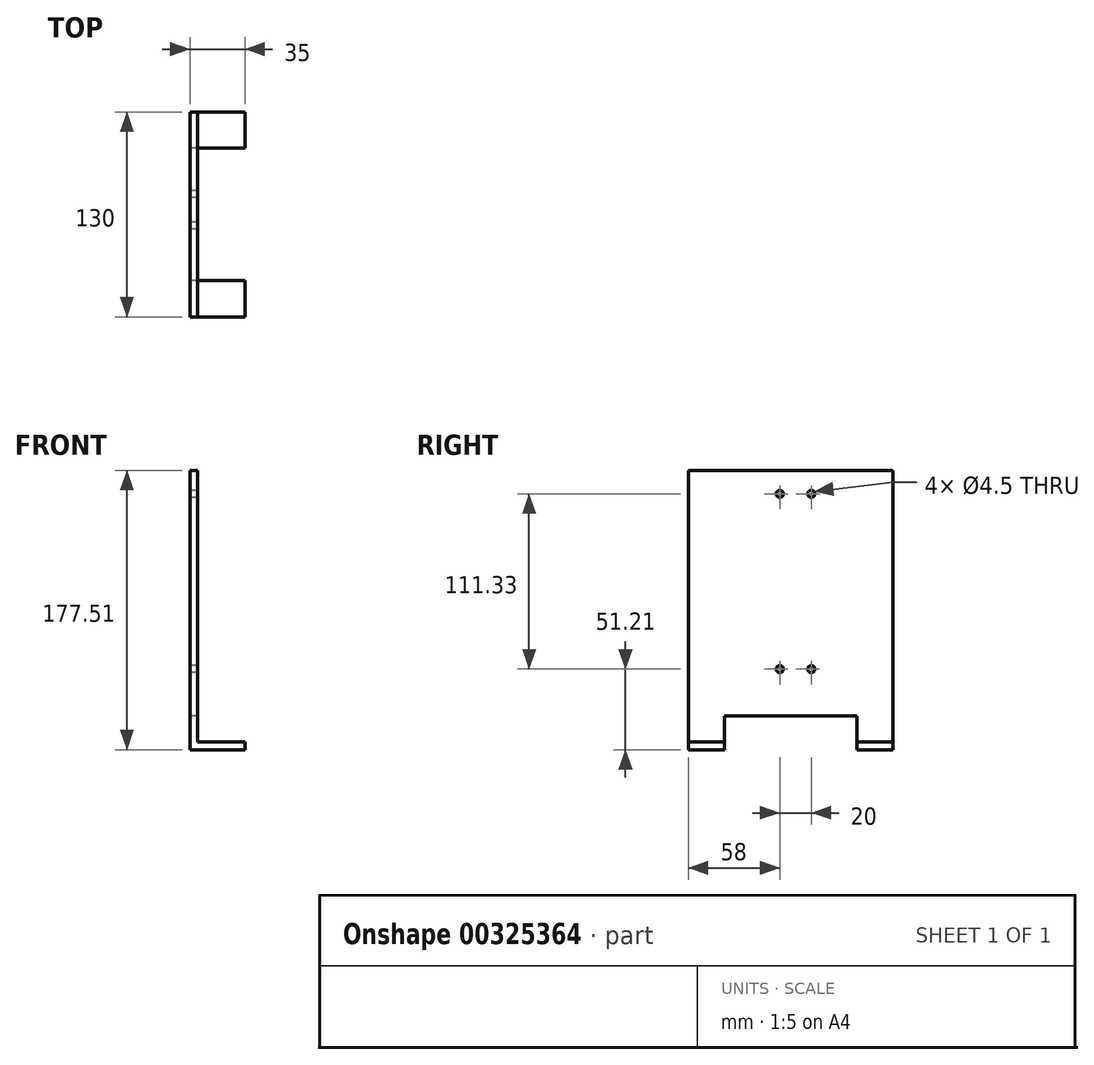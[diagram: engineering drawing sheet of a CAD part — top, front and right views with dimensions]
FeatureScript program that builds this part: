
annotation { "Feature Type Name" : "Feature", "Feature Type Description" : "" }
export const myFeature = defineFeature(function(context is Context, id is Id, definition is map)
    precondition{}
    {
        {
            var Q0;
            Q0=qCreatedBy(makeId("Right.planeOp"),FACE);
            var sketch = newSketch(context, id + "F0", { "sketchPlane" : qUnion([Q0])});
            skLineSegment(sketch, "E0.bottom", {"start": v(-38.4, 65.5) * mm, "end": v(32.4, 65.5) * mm, "construction": true});
            skLineSegment(sketch, "E0.top", {"start": v(-38.4, -65.5) * mm, "end": v(32.4, -65.5) * mm, "construction": true});
            skLineSegment(sketch, "E0.left", {"start": v(-48, 55.9) * mm, "end": v(-48, -55.9) * mm, "construction": true});
            skLineSegment(sketch, "E0.right", {"start": v(42, 55.9) * mm, "end": v(42, -55.9) * mm, "construction": true});
            skCircle(sketch, "E1", {"center": v(-10, 55.53) * mm, "radius": 2.25 * mm});
            skCircle(sketch, "E2", {"center": v(-10, -55.8) * mm, "radius": 2.25 * mm});
            skLineSegment(sketch, "E3", {"start": v(-10, 55.53) * mm, "end": v(-10, -55.8) * mm, "construction": true});
            skCircle(sketch, "E4.MirrorC", {"center": v(10, 55.53) * mm, "radius": 2.25 * mm});
            skCircle(sketch, "E5.MirrorC", {"center": v(10, -55.8) * mm, "radius": 2.25 * mm});
            skPoint(sketch, "E6.visualSharp", {"position": v(-48, 65.5) * mm});
            skArc(sketch, "E6.filletArc", {"start": v(-38.4, 65.5) * mm, "mid": v(-45.19, 62.69) * mm, "end": v(-48, 55.9) * mm, "construction": true});
            skPoint(sketch, "E7.visualSharp", {"position": v(42, -65.5) * mm});
            skArc(sketch, "E7.filletArc", {"start": v(32.4, -65.5) * mm, "mid": v(39.19, -62.69) * mm, "end": v(42, -55.9) * mm, "construction": true});
            skPoint(sketch, "E8.visualSharp", {"position": v(42, 65.5) * mm});
            skArc(sketch, "E8.filletArc", {"start": v(42, 55.9) * mm, "mid": v(39.19, 62.69) * mm, "end": v(32.4, 65.5) * mm, "construction": true});
            skPoint(sketch, "E9.visualSharp", {"position": v(-48, -65.5) * mm});
            skArc(sketch, "E9.filletArc", {"start": v(-48, -55.9) * mm, "mid": v(-45.19, -62.69) * mm, "end": v(-38.4, -65.5) * mm, "construction": true});
            skLineSegment(sketch, "E10.bottom", {"start": v(-68, 70.5) * mm, "end": v(62, 70.5) * mm});
            skLineSegment(sketch, "E10.top", {"start": v(-45.1, -85.5) * mm, "end": v(39.1, -85.5) * mm});
            skLineSegment(sketch, "E10.left", {"start": v(-68, 70.5) * mm, "end": v(-68, -85.5) * mm});
            skLineSegment(sketch, "E10.right", {"start": v(62, 70.5) * mm, "end": v(62, -85.5) * mm});
            skLineSegment(sketch, "E11.top", {"start": v(-68, -107) * mm, "end": v(-45.1, -107) * mm});
            skLineSegment(sketch, "E11.left", {"start": v(-68, -85.5) * mm, "end": v(-68, -107) * mm});
            skLineSegment(sketch, "E11.right", {"start": v(-45.1, -85.5) * mm, "end": v(-45.1, -107) * mm});
            skLineSegment(sketch, "E12", {"start": v(-3, -85.5) * mm, "end": v(-3, 70.5) * mm, "construction": true});
            skLineSegment(sketch, "E13.MirrorCS", {"start": v(62, -85.5) * mm, "end": v(62, -107) * mm});
            skLineSegment(sketch, "E14.MirrorCS", {"start": v(39.1, -85.5) * mm, "end": v(39.1, -107) * mm});
            skLineSegment(sketch, "E15.MirrorCS", {"start": v(62, -107) * mm, "end": v(39.1, -107) * mm});
            skSolve(sketch);
        }
        {
            var Q0;
            Q0=makeQuery(id+"F0.imprint","IMPRINT",FACE,{"disambiguationData":[TD([[makeQuery(id+"F0.imprint","IMPRINT",EDGE,{"derivedFrom":sQuery(id+"F0.wireOp",EDGE,"E1")}),-1.0]])]});
            extrude(context, id + "F1", {"entities" : qUnion([Q0]), "depth" : 5 * mm});
        }
        {
            var Q0;
            Q0=makeQuery(id+"F1.opExtrude","CAP_FACE",FACE,{"disambiguationData":[OSD([sQuery(id+"F0.wireOp",EDGE,"E1"),sQuery(id+"F0.wireOp",EDGE,"E2"),sQuery(id+"F0.wireOp",EDGE,"E4.MirrorC"),sQuery(id+"F0.wireOp",EDGE,"E5.MirrorC"),sQuery(id+"F0.wireOp",EDGE,"E10.bottom"),sQuery(id+"F0.wireOp",EDGE,"E10.top"),sQuery(id+"F0.wireOp",EDGE,"E10.left"),sQuery(id+"F0.wireOp",EDGE,"E10.right"),sQuery(id+"F0.wireOp",EDGE,"E11.top"),sQuery(id+"F0.wireOp",EDGE,"E11.left"),sQuery(id+"F0.wireOp",EDGE,"E11.right"),sQuery(id+"F0.wireOp",EDGE,"E13.MirrorCS"),sQuery(id+"F0.wireOp",EDGE,"E14.MirrorCS"),sQuery(id+"F0.wireOp",EDGE,"E15.MirrorCS")])],"isStart":false});
            var sketch = newSketch(context, id + "F2", { "sketchPlane" : qUnion([Q0])});
            skLineSegment(sketch, "E16.bottom", {"start": v(-45.1, -107) * mm, "end": v(-68, -107) * mm});
            skLineSegment(sketch, "E16.top", {"start": v(-45.1, -102) * mm, "end": v(-68, -102) * mm});
            skLineSegment(sketch, "E16.left", {"start": v(-45.1, -107) * mm, "end": v(-45.1, -102) * mm});
            skLineSegment(sketch, "E16.right", {"start": v(-68, -107) * mm, "end": v(-68, -102) * mm});
            skLineSegment(sketch, "E17.bottom", {"start": v(39.1, -107) * mm, "end": v(62, -107) * mm});
            skLineSegment(sketch, "E17.top", {"start": v(39.1, -102) * mm, "end": v(62, -102) * mm});
            skLineSegment(sketch, "E17.left", {"start": v(39.1, -107) * mm, "end": v(39.1, -102) * mm});
            skLineSegment(sketch, "E17.right", {"start": v(62, -107) * mm, "end": v(62, -102) * mm});
            skSolve(sketch);
        }
        {
            var Q0;
            Q0=makeQuery(id+"F2.imprint","IMPRINT",FACE,{"disambiguationData":[TD([[makeQuery(id+"F2.imprint","IMPRINT",EDGE,{"derivedFrom":sQuery(id+"F2.wireOp",EDGE,"E16.bottom")}),1.0]])]});
            var Q1;
            Q1=makeQuery(id+"F2.imprint","IMPRINT",FACE,{"disambiguationData":[TD([[makeQuery(id+"F2.imprint","IMPRINT",EDGE,{"derivedFrom":sQuery(id+"F2.wireOp",EDGE,"E17.bottom")}),-1.0]])]});
            extrude(context, id + "F3", {"entities" : qUnion([Q0, Q1]), "operationType" : NewBodyOperationType.ADD, "depth" : 30 * mm});
        }
    });
